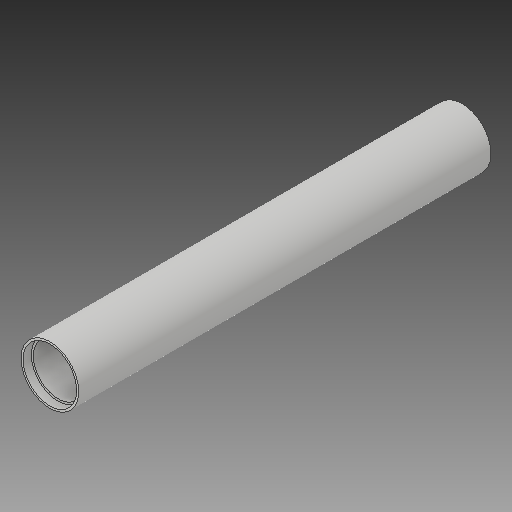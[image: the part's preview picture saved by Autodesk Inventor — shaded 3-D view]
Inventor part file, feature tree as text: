
AUTODESK INVENTOR PART (.ipt)
format: ipt  version: 2019 (Build 230136000, 136)  size: 110,080 bytes
history: native  units: mm
features: extrude x4, sketch x4
ambient origin geometry x8: Origin, YZ Plane, XZ Plane, XY Plane, X Axis, Y Axis, Z Axis, Center Point
bodies: Solid1 (feature_tree)
feature tree (8):
  extrude  "Extrusion1"  Depth=500.0mm TaperAngle=0.0deg
  extrude  "Extrusion2"  Depth=10.0mm TaperAngle=0.0deg
  extrude  "Extrusion3"  Depth=10.0mm TaperAngle=0.0deg
  extrude  "Extrusion4"  Depth=500.0mm TaperAngle=0.0deg
  sketch  "Sketch1"  dims[d0=70.0mm d1=500.0mm d2=0.0mm]
  sketch  "Sketch2"  dims[d3=65.0mm d4=10.0mm d5=0.0mm]
  sketch  "Sketch3"  dims[d6=65.0mm d7=10.0mm d8=0.0mm]
  sketch  "Sketch4"  dims[d9=60.0mm d10=500.0mm d11=0.0mm]
